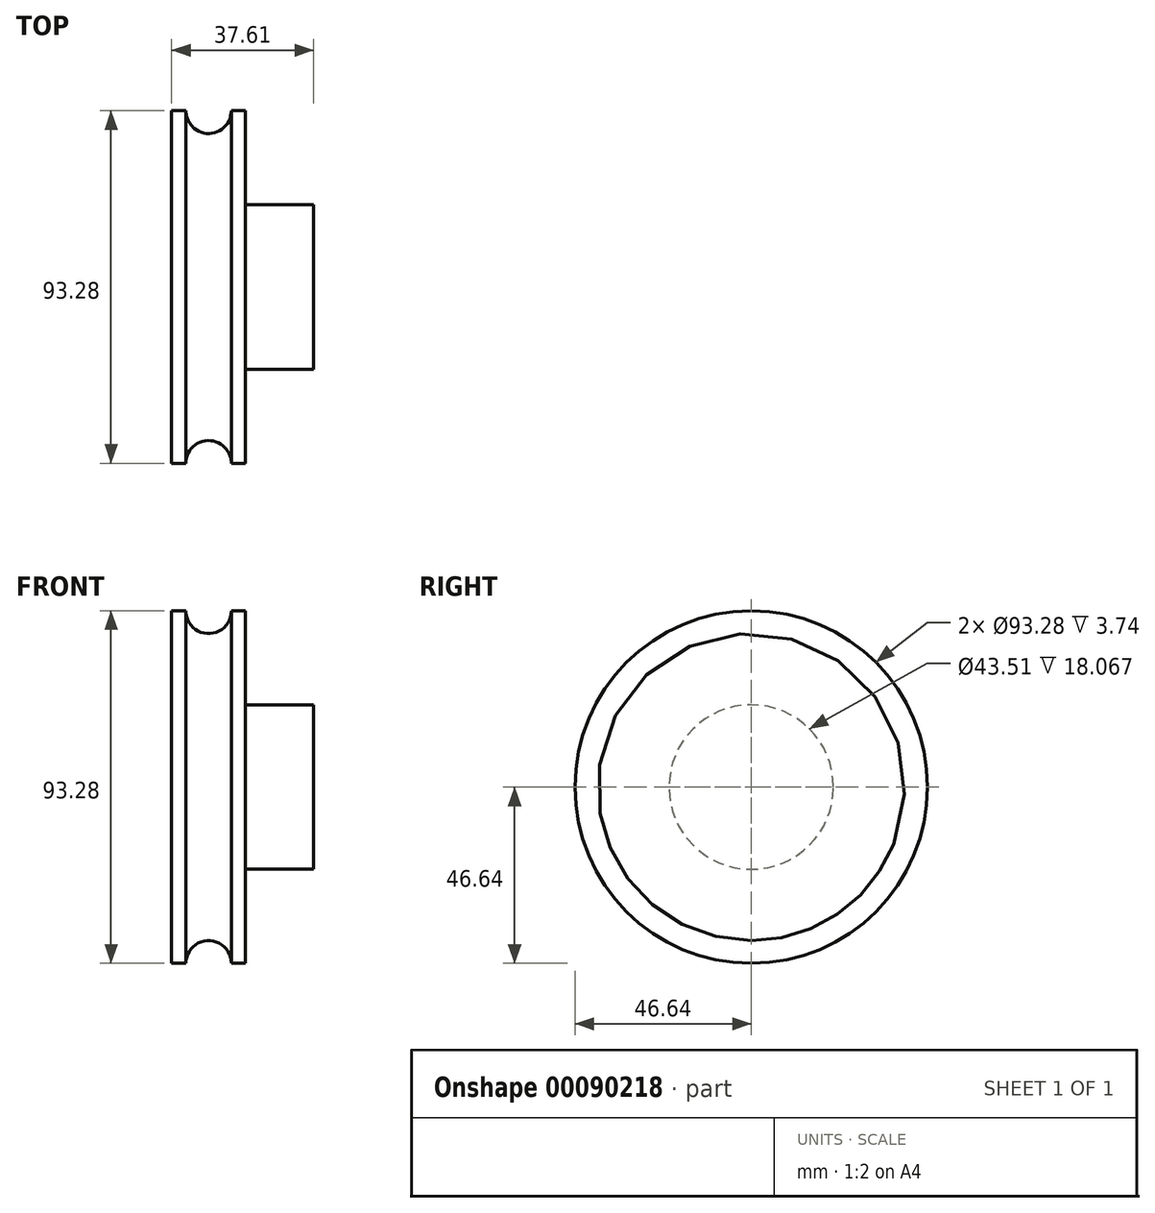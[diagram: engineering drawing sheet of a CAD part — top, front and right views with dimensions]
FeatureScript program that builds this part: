
annotation { "Feature Type Name" : "Feature", "Feature Type Description" : "" }
export const myFeature = defineFeature(function(context is Context, id is Id, definition is map)
    precondition{}
    {
        {
            var Q0;
            Q0=qCreatedBy(makeId("Front.planeOp"),FACE);
            var sketch = newSketch(context, id + "F0", { "sketchPlane" : qUnion([Q0])});
            skLineSegment(sketch, "E0", {"start": v(0, 0) * mm, "end": v(0, 46.64) * mm});
            skLineSegment(sketch, "E1", {"start": v(0, 46.64) * mm, "end": v(3.74, 46.64) * mm});
            skLineSegment(sketch, "E2", {"start": v(19.54, 46.64) * mm, "end": v(19.54, 21.75) * mm});
            skLineSegment(sketch, "E3", {"start": v(19.54, 21.75) * mm, "end": v(37.6, 21.75) * mm});
            skLineSegment(sketch, "E4", {"start": v(37.6, 21.75) * mm, "end": v(37.6, 0) * mm});
            skLineSegment(sketch, "E5", {"start": v(-21.39, 0) * mm, "end": v(62.31, 0) * mm, "construction": true});
            skArc(sketch, "E6", {"start": v(3.74, 46.64) * mm, "mid": v(9.77, 40.61) * mm, "end": v(15.8, 46.64) * mm});
            skLineSegment(sketch, "E7.trimOffspring", {"start": v(15.8, 46.64) * mm, "end": v(19.54, 46.64) * mm});
            skSolve(sketch);
        }
        {
            var Q0;
            Q0=sQuery(id+"F0.wireOp",EDGE,"E5");
            var Q1;
            Q1=sQuery(id+"F0.wireOp",EDGE,"E1");
            var Q2;
            Q2=sQuery(id+"F0.wireOp",EDGE,"E2");
            var Q3;
            Q3=sQuery(id+"F0.wireOp",EDGE,"E3");
            var Q4;
            Q4=sQuery(id+"F0.wireOp",EDGE,"E4");
            var Q5;
            Q5=sQuery(id+"F0.wireOp",EDGE,"E0");
            var Q6;
            Q6=sQuery(id+"F0.wireOp",EDGE,"E6");
            var Q7;
            Q7=sQuery(id+"F0.wireOp",EDGE,"E7.trimOffspring");
            var Q8;
            Q8=sQuery(id+"F0.wireOp",EDGE,"E5");
            revolve(context, id + "F1", {"bodyType" : ToolBodyType.SURFACE, "surfaceEntities" : qUnion([Q0, Q1, Q2, Q3, Q4, Q5, Q6, Q7]), "axis" : qUnion([Q8]), "revolveType" : RevolveType.FULL});
        }
    });
